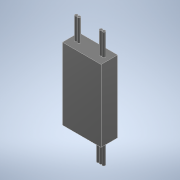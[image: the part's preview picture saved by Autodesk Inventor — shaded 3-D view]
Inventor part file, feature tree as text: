
AUTODESK INVENTOR PART (.ipt)
format: ipt  version: 2022 (Build 260153000, 153)  size: 125,440 bytes
history: native  units: in
note: dims shown in document units (in); Inventor stores cm internally (conversion verified against a paired STEP export)
features: extrude x3, sketch x3
ambient origin geometry x8: Origin, YZ Plane, XZ Plane, XY Plane, X Axis, Y Axis, Z Axis, Center Point
bodies: Solid1 (feature_tree)
feature tree (6):
  extrude  "Extrusion1"  Depth=1.5354in
  extrude  "Extrusion2"  Depth=0.4724in TaperAngle=0.0deg
  extrude  "Extrusion3"  Depth=0.4724in
  sketch  "Sketch1"  dims[d0=0.8268in d1=1.5354in]
  sketch  "Sketch2"  dims[d2=0.3543in d3=0.0in d7=0.4724in d8=0.0in]
  sketch  "Sketch3"  dims[d12=0.4724in d13=0.0in d14=0.0591in d15=0.0591in d16=0.0591in d17=0.1181in d18=0.1181in d19=0.0591in d20=0.0591in d21=0.0591in d22=0.1181in]
